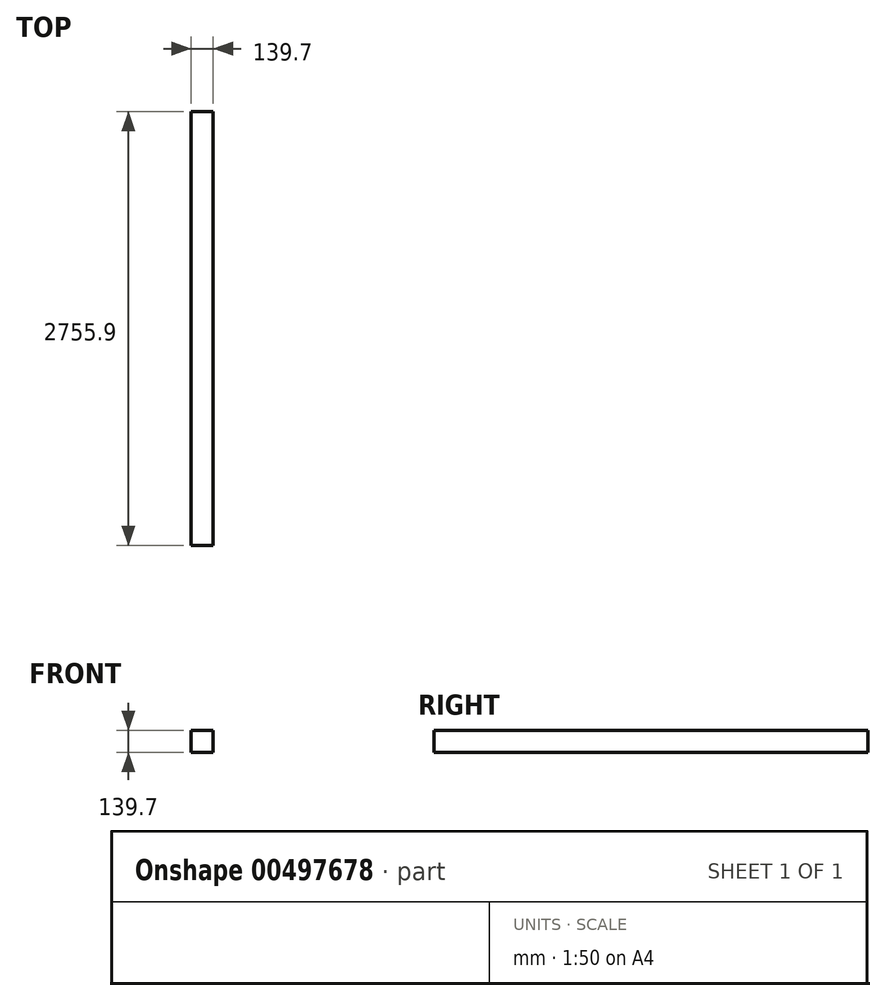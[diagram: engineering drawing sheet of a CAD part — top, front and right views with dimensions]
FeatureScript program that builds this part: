
annotation { "Feature Type Name" : "Feature", "Feature Type Description" : "" }
export const myFeature = defineFeature(function(context is Context, id is Id, definition is map)
    precondition{}
    {
        {
            var Q0;
            Q0=qCreatedBy(makeId("Front.planeOp"),FACE);
            var sketch = newSketch(context, id + "F0", { "sketchPlane" : qUnion([Q0])});
            skLineSegment(sketch, "E0.bottom", {"start": v(0, 0) * mm, "end": v(139.7, 0) * mm});
            skLineSegment(sketch, "E0.top", {"start": v(0, 139.7) * mm, "end": v(139.7, 139.7) * mm});
            skLineSegment(sketch, "E0.left", {"start": v(0, 0) * mm, "end": v(0, 139.7) * mm});
            skLineSegment(sketch, "E0.right", {"start": v(139.7, 0) * mm, "end": v(139.7, 139.7) * mm});
            skSolve(sketch);
        }
        {
            var Q0;
            Q0 = qSketchRegion(id + "F0", true);
            extrude(context, id + "F1", {"entities" : qUnion([Q0]), "depth" : 2755.9 * mm});
        }
    });
